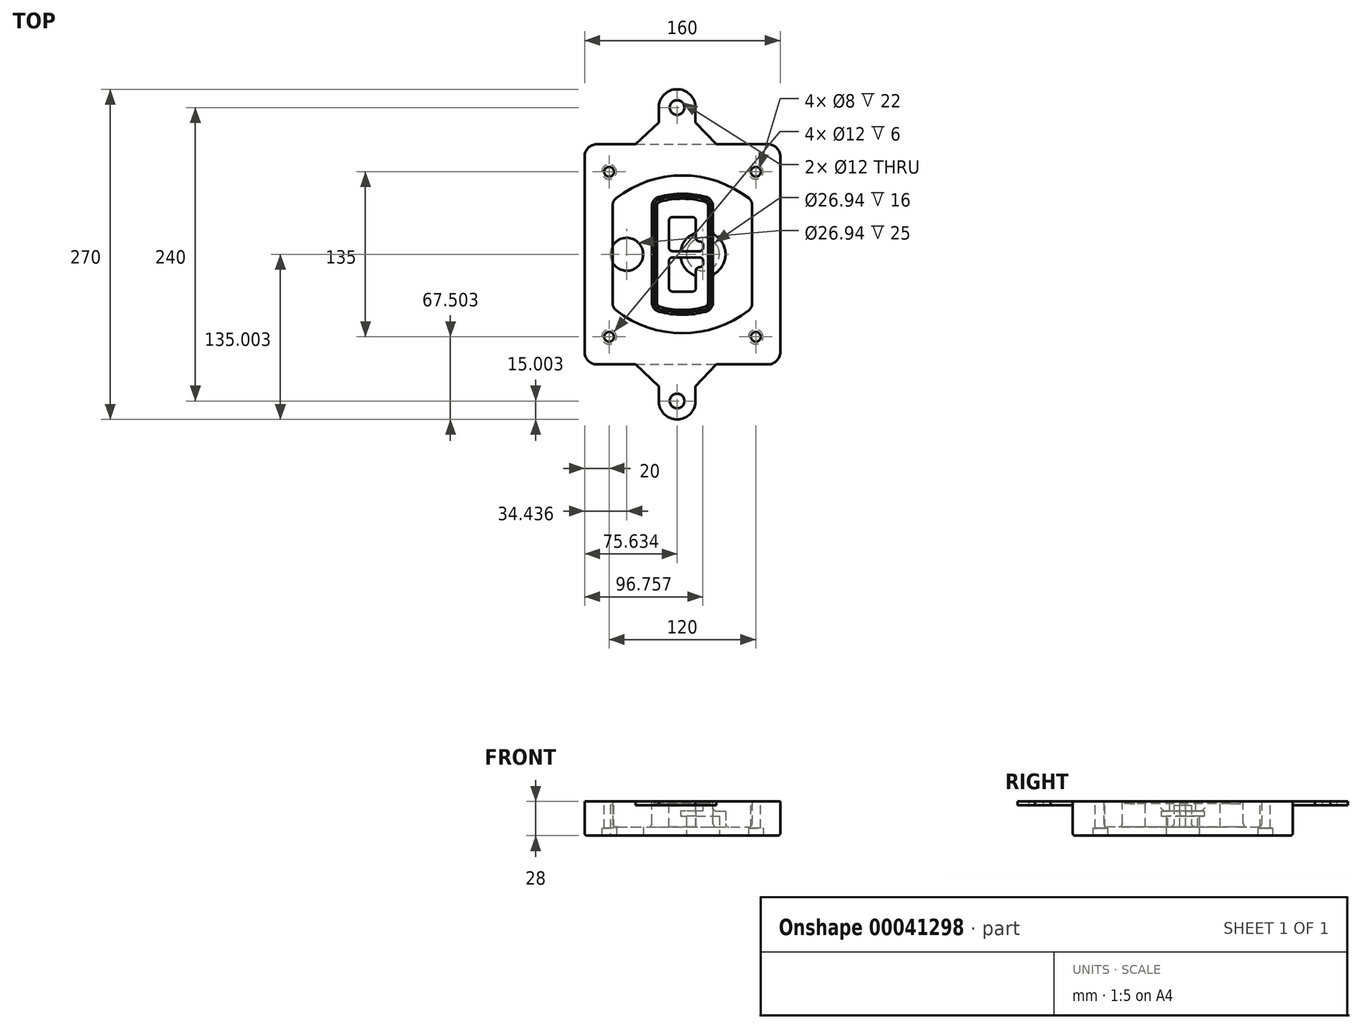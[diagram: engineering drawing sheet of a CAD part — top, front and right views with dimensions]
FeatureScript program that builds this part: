
annotation { "Feature Type Name" : "Feature", "Feature Type Description" : "" }
export const myFeature = defineFeature(function(context is Context, id is Id, definition is map)
    precondition{}
    {
        {
            var Q0;
            Q0=qCreatedBy(makeId("Top.planeOp"),FACE);
            var sketch = newSketch(context, id + "F0", { "sketchPlane" : qUnion([Q0])});
            skPoint(sketch, "E0.rect.middle", {"position": v(0, 0) * mm});
            skLineSegment(sketch, "E1.bottom", {"start": v(24.05, 28.38) * mm, "end": v(164.05, 28.38) * mm});
            skLineSegment(sketch, "E1.top", {"start": v(24.05, 208.38) * mm, "end": v(164.05, 208.38) * mm});
            skLineSegment(sketch, "E1.left", {"start": v(14.05, 38.38) * mm, "end": v(14.05, 198.38) * mm});
            skLineSegment(sketch, "E1.right", {"start": v(174.05, 38.38) * mm, "end": v(174.05, 198.38) * mm});
            skLineSegment(sketch, "E2", {"start": v(14.05, 208.38) * mm, "end": v(174.05, 28.38) * mm, "construction": true});
            skLineSegment(sketch, "E3", {"start": v(174.05, 208.38) * mm, "end": v(14.05, 28.38) * mm, "construction": true});
            skCircle(sketch, "E4", {"center": v(34.05, 185.88) * mm, "radius": 4 * mm});
            skCircle(sketch, "E5", {"center": v(154.05, 185.88) * mm, "radius": 4 * mm});
            skCircle(sketch, "E6", {"center": v(154.05, 50.88) * mm, "radius": 4 * mm});
            skCircle(sketch, "E7", {"center": v(34.05, 50.88) * mm, "radius": 4 * mm});
            skLineSegment(sketch, "E8", {"start": v(34.05, 185.88) * mm, "end": v(154.05, 185.88) * mm, "construction": true});
            skLineSegment(sketch, "E9", {"start": v(154.05, 185.88) * mm, "end": v(154.05, 50.88) * mm, "construction": true});
            skLineSegment(sketch, "E10", {"start": v(154.05, 50.88) * mm, "end": v(34.05, 50.88) * mm, "construction": true});
            skLineSegment(sketch, "E11", {"start": v(34.05, 50.88) * mm, "end": v(34.05, 185.88) * mm, "construction": true});
            skLineSegment(sketch, "E12", {"start": v(34.05, 158.68) * mm, "end": v(34.05, 78.09) * mm});
            skLineSegment(sketch, "E13", {"start": v(154.05, 158.68) * mm, "end": v(154.05, 78.09) * mm});
            skArc(sketch, "E14", {"start": v(150.2, 166.56) * mm, "mid": v(94.05, 185.88) * mm, "end": v(37.9, 166.56) * mm});
            skArc(sketch, "E15", {"start": v(37.9, 70.2) * mm, "mid": v(94.05, 50.88) * mm, "end": v(150.2, 70.2) * mm});
            skLineSegment(sketch, "E16", {"start": v(34.05, 118.38) * mm, "end": v(154.05, 118.38) * mm, "construction": true});
            skPoint(sketch, "E17.visualSharp", {"position": v(34.05, 73.38) * mm});
            skArc(sketch, "E17.filletArc", {"start": v(34.05, 78.09) * mm, "mid": v(35.06, 73.7) * mm, "end": v(37.9, 70.2) * mm});
            skPoint(sketch, "E18.visualSharp", {"position": v(34.05, 163.38) * mm});
            skArc(sketch, "E18.filletArc", {"start": v(37.9, 166.56) * mm, "mid": v(35.06, 163.06) * mm, "end": v(34.05, 158.68) * mm});
            skPoint(sketch, "E19.visualSharp", {"position": v(154.05, 163.38) * mm});
            skArc(sketch, "E19.filletArc", {"start": v(154.05, 158.68) * mm, "mid": v(153.04, 163.06) * mm, "end": v(150.2, 166.56) * mm});
            skPoint(sketch, "E20.visualSharp", {"position": v(154.05, 73.38) * mm});
            skArc(sketch, "E20.filletArc", {"start": v(150.2, 70.2) * mm, "mid": v(153.04, 73.7) * mm, "end": v(154.05, 78.09) * mm});
            skPoint(sketch, "E21.visualSharp", {"position": v(14.05, 208.38) * mm});
            skArc(sketch, "E21.filletArc", {"start": v(24.05, 208.38) * mm, "mid": v(16.98, 205.45) * mm, "end": v(14.05, 198.38) * mm});
            skPoint(sketch, "E22.visualSharp", {"position": v(174.05, 208.38) * mm});
            skArc(sketch, "E22.filletArc", {"start": v(174.05, 198.38) * mm, "mid": v(171.12, 205.45) * mm, "end": v(164.05, 208.38) * mm});
            skPoint(sketch, "E23.visualSharp", {"position": v(174.05, 28.38) * mm});
            skArc(sketch, "E23.filletArc", {"start": v(164.05, 28.38) * mm, "mid": v(171.12, 31.31) * mm, "end": v(174.05, 38.38) * mm});
            skPoint(sketch, "E24.visualSharp", {"position": v(14.05, 28.38) * mm});
            skArc(sketch, "E24.filletArc", {"start": v(14.05, 38.38) * mm, "mid": v(16.98, 31.31) * mm, "end": v(24.05, 28.38) * mm});
            skArc(sketch, "E25.0", {"start": v(151.05, 158.68) * mm, "mid": v(150.34, 161.75) * mm, "end": v(148.36, 164.2) * mm});
            skLineSegment(sketch, "E25.1", {"start": v(151.05, 158.68) * mm, "end": v(151.05, 78.09) * mm});
            skArc(sketch, "E25.2", {"start": v(148.36, 72.57) * mm, "mid": v(150.34, 75.02) * mm, "end": v(151.05, 78.09) * mm});
            skArc(sketch, "E25.3", {"start": v(39.74, 72.57) * mm, "mid": v(94.05, 53.88) * mm, "end": v(148.36, 72.57) * mm});
            skArc(sketch, "E25.4", {"start": v(37.05, 78.09) * mm, "mid": v(37.76, 75.02) * mm, "end": v(39.74, 72.57) * mm});
            skArc(sketch, "E25.5", {"start": v(148.36, 164.2) * mm, "mid": v(94.05, 182.88) * mm, "end": v(39.74, 164.2) * mm});
            skLineSegment(sketch, "E25.6", {"start": v(37.05, 158.68) * mm, "end": v(37.05, 78.09) * mm});
            skArc(sketch, "E25.7", {"start": v(39.74, 164.2) * mm, "mid": v(37.76, 161.75) * mm, "end": v(37.05, 158.68) * mm});
            skArc(sketch, "E26.0", {"start": v(35.43, 169.71) * mm, "mid": v(31.47, 164.82) * mm, "end": v(30.05, 158.68) * mm});
            skArc(sketch, "E26.1", {"start": v(152.67, 169.71) * mm, "mid": v(94.05, 189.88) * mm, "end": v(35.43, 169.71) * mm});
            skArc(sketch, "E26.2", {"start": v(158.05, 158.68) * mm, "mid": v(156.63, 164.82) * mm, "end": v(152.67, 169.71) * mm});
            skLineSegment(sketch, "E26.3", {"start": v(158.05, 158.68) * mm, "end": v(158.05, 78.09) * mm});
            skArc(sketch, "E26.4", {"start": v(152.67, 67.05) * mm, "mid": v(156.63, 71.95) * mm, "end": v(158.05, 78.09) * mm});
            skLineSegment(sketch, "E26.5", {"start": v(30.05, 158.68) * mm, "end": v(30.05, 78.09) * mm});
            skArc(sketch, "E26.6", {"start": v(35.43, 67.05) * mm, "mid": v(94.05, 46.88) * mm, "end": v(152.67, 67.05) * mm});
            skArc(sketch, "E26.7", {"start": v(30.05, 78.09) * mm, "mid": v(31.47, 71.95) * mm, "end": v(35.43, 67.05) * mm});
            skSolve(sketch);
        }
        {
            var Q0;
            Q0=makeQuery(id+"F0.imprint","IMPRINT",FACE,{"disambiguationData":[TD([[makeQuery(id+"F0.imprint","IMPRINT",EDGE,{"derivedFrom":sQuery(id+"F0.wireOp",EDGE,"E1.bottom")}),1.0]])]});
            var Q1;
            Q1=makeQuery(id+"F0.imprint","IMPRINT",FACE,{"disambiguationData":[TD([[makeQuery(id+"F0.imprint","IMPRINT",EDGE,{"derivedFrom":sQuery(id+"F0.wireOp",EDGE,"E12")}),1.0]])]});
            var Q2;
            Q2=makeQuery(id+"F0.imprint","IMPRINT",FACE,{"disambiguationData":[TD([[makeQuery(id+"F0.imprint","IMPRINT",EDGE,{"derivedFrom":sQuery(id+"F0.wireOp",EDGE,"E25.0")}),1.0]])]});
            var Q3;
            Q3=makeQuery(id+"F0.imprint","IMPRINT",FACE,{"disambiguationData":[TD([[makeQuery(id+"F0.imprint","IMPRINT",EDGE,{"derivedFrom":sQuery(id+"F0.wireOp",EDGE,"E12")}),-1.0]])]});
            extrude(context, id + "F1", {"entities" : qUnion([Q0, Q1, Q2, Q3]), "oppositeDirection" : true, "depth" : 25 * mm});
        }
        {
            var Q0;
            Q0=makeQuery(id+"F0.imprint","IMPRINT",FACE,{"disambiguationData":[TD([[makeQuery(id+"F0.imprint","IMPRINT",EDGE,{"derivedFrom":sQuery(id+"F0.wireOp",EDGE,"E12")}),1.0]])]});
            extrude(context, id + "F2", {"entities" : qUnion([Q0]), "operationType" : NewBodyOperationType.ADD, "depth" : 3 * mm});
        }
        {
            var Q0;
            Q0=makeQuery(id+"F0.imprint","IMPRINT",FACE,{"disambiguationData":[TD([[makeQuery(id+"F0.imprint","IMPRINT",EDGE,{"derivedFrom":sQuery(id+"F0.wireOp",EDGE,"E25.0")}),1.0]])]});
            extrude(context, id + "F3", {"entities" : qUnion([Q0]), "operationType" : NewBodyOperationType.REMOVE, "oppositeDirection" : true, "depth" : 18 * mm});
        }
        {
            var Q0;
            Q0=makeQuery(id+"F2.opExtrude","CAP_FACE",FACE,{"disambiguationData":[OSD([sQuery(id+"F0.wireOp",EDGE,"E12"),sQuery(id+"F0.wireOp",EDGE,"E13"),sQuery(id+"F0.wireOp",EDGE,"E14"),sQuery(id+"F0.wireOp",EDGE,"E15"),sQuery(id+"F0.wireOp",EDGE,"E17.filletArc"),sQuery(id+"F0.wireOp",EDGE,"E18.filletArc"),sQuery(id+"F0.wireOp",EDGE,"E19.filletArc"),sQuery(id+"F0.wireOp",EDGE,"E20.filletArc"),sQuery(id+"F0.wireOp",EDGE,"E25.0"),sQuery(id+"F0.wireOp",EDGE,"E25.1"),sQuery(id+"F0.wireOp",EDGE,"E25.2"),sQuery(id+"F0.wireOp",EDGE,"E25.3"),sQuery(id+"F0.wireOp",EDGE,"E25.4"),sQuery(id+"F0.wireOp",EDGE,"E25.5"),sQuery(id+"F0.wireOp",EDGE,"E25.6"),sQuery(id+"F0.wireOp",EDGE,"E25.7")])],"isStart":false});
            var sketch = newSketch(context, id + "F4", { "sketchPlane" : qUnion([Q0])});
            skArc(sketch, "E27.0", {"start": v(74.97, 71.41) * mm, "mid": v(94.05, 68.88) * mm, "end": v(113.13, 71.41) * mm});
            skArc(sketch, "E28.0", {"start": v(113.13, 165.35) * mm, "mid": v(94.05, 167.88) * mm, "end": v(74.97, 165.35) * mm});
            skLineSegment(sketch, "E29", {"start": v(69.05, 157.63) * mm, "end": v(69.05, 79.14) * mm});
            skLineSegment(sketch, "E30", {"start": v(119.05, 157.63) * mm, "end": v(119.05, 79.14) * mm});
            skLineSegment(sketch, "E31", {"start": v(69.05, 163.48) * mm, "end": v(119.05, 163.48) * mm, "construction": true});
            skLineSegment(sketch, "E32", {"start": v(69.05, 73.28) * mm, "end": v(119.05, 73.28) * mm, "construction": true});
            skPoint(sketch, "E33.visualSharp", {"position": v(69.05, 163.48) * mm});
            skArc(sketch, "E33.filletArc", {"start": v(74.97, 165.35) * mm, "mid": v(70.7, 162.5) * mm, "end": v(69.05, 157.63) * mm});
            skPoint(sketch, "E34.visualSharp", {"position": v(119.05, 163.48) * mm});
            skArc(sketch, "E34.filletArc", {"start": v(119.05, 157.63) * mm, "mid": v(117.4, 162.5) * mm, "end": v(113.13, 165.35) * mm});
            skPoint(sketch, "E35.visualSharp", {"position": v(119.05, 73.28) * mm});
            skArc(sketch, "E35.filletArc", {"start": v(113.13, 71.41) * mm, "mid": v(117.4, 74.27) * mm, "end": v(119.05, 79.14) * mm});
            skPoint(sketch, "E36.visualSharp", {"position": v(69.05, 73.28) * mm});
            skArc(sketch, "E36.filletArc", {"start": v(69.05, 79.14) * mm, "mid": v(70.7, 74.27) * mm, "end": v(74.97, 71.41) * mm});
            skArc(sketch, "E37.0", {"start": v(148.36, 164.2) * mm, "mid": v(94.05, 182.88) * mm, "end": v(39.74, 164.2) * mm});
            skArc(sketch, "E37.1", {"start": v(39.74, 164.2) * mm, "mid": v(37.76, 161.75) * mm, "end": v(37.05, 158.68) * mm});
            skLineSegment(sketch, "E37.2", {"start": v(37.05, 158.68) * mm, "end": v(37.05, 78.09) * mm});
            skArc(sketch, "E37.3", {"start": v(37.05, 78.09) * mm, "mid": v(37.76, 75.02) * mm, "end": v(39.74, 72.57) * mm});
            skArc(sketch, "E37.4", {"start": v(39.74, 72.57) * mm, "mid": v(94.05, 53.88) * mm, "end": v(148.36, 72.57) * mm});
            skArc(sketch, "E37.5", {"start": v(148.36, 72.57) * mm, "mid": v(150.34, 75.02) * mm, "end": v(151.05, 78.09) * mm});
            skLineSegment(sketch, "E37.6", {"start": v(151.05, 158.68) * mm, "end": v(151.05, 78.09) * mm});
            skArc(sketch, "E37.7", {"start": v(151.05, 158.68) * mm, "mid": v(150.34, 161.75) * mm, "end": v(148.36, 164.2) * mm});
            skLineSegment(sketch, "E38.0", {"start": v(117.05, 157.63) * mm, "end": v(117.05, 79.14) * mm});
            skArc(sketch, "E38.1", {"start": v(112.61, 73.34) * mm, "mid": v(115.81, 75.49) * mm, "end": v(117.05, 79.14) * mm});
            skArc(sketch, "E38.2", {"start": v(75.49, 73.34) * mm, "mid": v(94.05, 70.88) * mm, "end": v(112.61, 73.34) * mm});
            skArc(sketch, "E38.3", {"start": v(71.05, 79.14) * mm, "mid": v(72.29, 75.49) * mm, "end": v(75.49, 73.34) * mm});
            skLineSegment(sketch, "E38.4", {"start": v(71.05, 157.63) * mm, "end": v(71.05, 79.14) * mm});
            skArc(sketch, "E38.5", {"start": v(117.05, 157.63) * mm, "mid": v(115.81, 161.28) * mm, "end": v(112.61, 163.42) * mm});
            skArc(sketch, "E38.6", {"start": v(75.49, 163.42) * mm, "mid": v(72.29, 161.28) * mm, "end": v(71.05, 157.63) * mm});
            skArc(sketch, "E38.7", {"start": v(112.61, 163.42) * mm, "mid": v(94.05, 165.88) * mm, "end": v(75.49, 163.42) * mm});
            skArc(sketch, "E39.0", {"start": v(115.05, 157.63) * mm, "mid": v(114.23, 160.06) * mm, "end": v(112.1, 161.5) * mm});
            skLineSegment(sketch, "E39.1", {"start": v(115.05, 157.63) * mm, "end": v(115.05, 79.14) * mm});
            skArc(sketch, "E39.2", {"start": v(112.1, 75.27) * mm, "mid": v(114.23, 76.7) * mm, "end": v(115.05, 79.14) * mm});
            skArc(sketch, "E39.3", {"start": v(76, 75.27) * mm, "mid": v(94.05, 72.88) * mm, "end": v(112.1, 75.27) * mm});
            skArc(sketch, "E39.4", {"start": v(73.05, 79.14) * mm, "mid": v(73.87, 76.7) * mm, "end": v(76, 75.27) * mm});
            skArc(sketch, "E39.5", {"start": v(112.1, 161.5) * mm, "mid": v(94.05, 163.88) * mm, "end": v(76, 161.5) * mm});
            skLineSegment(sketch, "E39.6", {"start": v(73.05, 157.63) * mm, "end": v(73.05, 79.14) * mm});
            skArc(sketch, "E39.7", {"start": v(76, 161.5) * mm, "mid": v(73.87, 160.06) * mm, "end": v(73.05, 157.63) * mm});
            skLineSegment(sketch, "E40", {"start": v(69.05, 118.38) * mm, "end": v(119.05, 118.38) * mm, "construction": true});
            skLineSegment(sketch, "E41", {"start": v(83.05, 123.88) * mm, "end": v(83.05, 145.88) * mm});
            skLineSegment(sketch, "E42", {"start": v(86.05, 148.88) * mm, "end": v(102.05, 148.88) * mm});
            skLineSegment(sketch, "E43", {"start": v(105.05, 145.88) * mm, "end": v(105.05, 131.88) * mm});
            skLineSegment(sketch, "E44", {"start": v(108.05, 128.88) * mm, "end": v(108.05, 128.88) * mm});
            skLineSegment(sketch, "E45", {"start": v(111.05, 125.88) * mm, "end": v(111.05, 123.88) * mm});
            skLineSegment(sketch, "E46", {"start": v(108.05, 120.88) * mm, "end": v(86.05, 120.88) * mm});
            skPoint(sketch, "E47.visualSharp", {"position": v(83.05, 148.88) * mm});
            skArc(sketch, "E47.filletArc", {"start": v(86.05, 148.88) * mm, "mid": v(83.93, 148) * mm, "end": v(83.05, 145.88) * mm});
            skPoint(sketch, "E48.visualSharp", {"position": v(105.05, 148.88) * mm});
            skArc(sketch, "E48.filletArc", {"start": v(105.05, 145.88) * mm, "mid": v(104.17, 148) * mm, "end": v(102.05, 148.88) * mm});
            skPoint(sketch, "E49.visualSharp", {"position": v(105.05, 128.88) * mm});
            skArc(sketch, "E49.filletArc", {"start": v(105.05, 131.88) * mm, "mid": v(105.93, 129.76) * mm, "end": v(108.05, 128.88) * mm});
            skPoint(sketch, "E50.visualSharp", {"position": v(111.05, 128.88) * mm});
            skArc(sketch, "E50.filletArc", {"start": v(111.05, 125.88) * mm, "mid": v(110.17, 128) * mm, "end": v(108.05, 128.88) * mm});
            skPoint(sketch, "E51.visualSharp", {"position": v(111.05, 120.88) * mm});
            skArc(sketch, "E51.filletArc", {"start": v(108.05, 120.88) * mm, "mid": v(110.17, 121.76) * mm, "end": v(111.05, 123.88) * mm});
            skPoint(sketch, "E52.visualSharp", {"position": v(83.05, 120.88) * mm});
            skArc(sketch, "E52.filletArc", {"start": v(83.05, 123.88) * mm, "mid": v(83.93, 121.76) * mm, "end": v(86.05, 120.88) * mm});
            skLineSegment(sketch, "E53.0.MirrorCS", {"start": v(108.05, 115.88) * mm, "end": v(86.05, 115.88) * mm});
            skArc(sketch, "E54.0.MirrorCS", {"start": v(83.05, 112.88) * mm, "mid": v(83.93, 115) * mm, "end": v(86.05, 115.88) * mm});
            skLineSegment(sketch, "E55.0.MirrorCS", {"start": v(83.05, 112.88) * mm, "end": v(83.05, 90.88) * mm});
            skArc(sketch, "E56.0.MirrorCS", {"start": v(86.05, 87.88) * mm, "mid": v(83.93, 88.76) * mm, "end": v(83.05, 90.88) * mm});
            skLineSegment(sketch, "E57.0.MirrorCS", {"start": v(86.05, 87.88) * mm, "end": v(102.05, 87.88) * mm});
            skArc(sketch, "E58.0.MirrorCS", {"start": v(105.05, 90.88) * mm, "mid": v(104.17, 88.76) * mm, "end": v(102.05, 87.88) * mm});
            skLineSegment(sketch, "E59.0.MirrorCS", {"start": v(105.05, 90.88) * mm, "end": v(105.05, 104.88) * mm});
            skArc(sketch, "E60.0.MirrorCS", {"start": v(105.05, 104.88) * mm, "mid": v(105.93, 107) * mm, "end": v(108.05, 107.88) * mm});
            skArc(sketch, "E61.0.MirrorCS", {"start": v(111.05, 110.88) * mm, "mid": v(110.17, 108.76) * mm, "end": v(108.05, 107.88) * mm});
            skLineSegment(sketch, "E62.0.MirrorCS", {"start": v(111.05, 110.88) * mm, "end": v(111.05, 112.88) * mm});
            skArc(sketch, "E63.0.MirrorCS", {"start": v(108.05, 115.88) * mm, "mid": v(110.17, 115) * mm, "end": v(111.05, 112.88) * mm});
            skSolve(sketch);
        }
        {
            var Q0;
            Q0=makeQuery(id+"F4.imprint","IMPRINT",FACE,{"disambiguationData":[TD([[makeQuery(id+"F4.imprint","IMPRINT",EDGE,{"derivedFrom":sQuery(id+"F4.wireOp",EDGE,"E27.0")}),1.0]])]});
            var Q1;
            Q1=makeQuery(id+"F4.imprint","IMPRINT",FACE,{"disambiguationData":[TD([[makeQuery(id+"F4.imprint","IMPRINT",EDGE,{"derivedFrom":sQuery(id+"F4.wireOp",EDGE,"E38.0")}),-1.0]])]});
            var Q2;
            Q2=makeQuery(id+"F4.imprint","IMPRINT",FACE,{"disambiguationData":[TD([[makeQuery(id+"F4.imprint","IMPRINT",EDGE,{"derivedFrom":sQuery(id+"F4.wireOp",EDGE,"E39.0")}),1.0]])]});
            extrude(context, id + "F5", {"entities" : qUnion([Q0, Q1, Q2]), "operationType" : NewBodyOperationType.ADD, "endBound" : BoundingType.UP_TO_NEXT, "oppositeDirection" : true, "depth" : 25 * mm});
        }
        {
            var Q0;
            Q0=makeQuery(id+"F4.imprint","IMPRINT",FACE,{"disambiguationData":[TD([[makeQuery(id+"F4.imprint","IMPRINT",EDGE,{"derivedFrom":sQuery(id+"F4.wireOp",EDGE,"E38.0")}),-1.0]])]});
            extrude(context, id + "F6", {"entities" : qUnion([Q0]), "operationType" : NewBodyOperationType.REMOVE, "oppositeDirection" : true, "depth" : 2 * mm});
        }
        {
            var Q0;
            Q0=makeQuery(id+"F1.opExtrude","CAP_FACE",FACE,{"disambiguationData":[OSD([sQuery(id+"F0.wireOp",EDGE,"E1.bottom"),sQuery(id+"F0.wireOp",EDGE,"E1.top"),sQuery(id+"F0.wireOp",EDGE,"E1.left"),sQuery(id+"F0.wireOp",EDGE,"E1.right"),sQuery(id+"F0.wireOp",EDGE,"E4"),sQuery(id+"F0.wireOp",EDGE,"E5"),sQuery(id+"F0.wireOp",EDGE,"E6"),sQuery(id+"F0.wireOp",EDGE,"E7"),sQuery(id+"F0.wireOp",EDGE,"E21.filletArc"),sQuery(id+"F0.wireOp",EDGE,"E22.filletArc"),sQuery(id+"F0.wireOp",EDGE,"E23.filletArc"),sQuery(id+"F0.wireOp",EDGE,"E24.filletArc")])],"isStart":false});
            var sketch = newSketch(context, id + "F7", { "sketchPlane" : qUnion([Q0])});
            skCircle(sketch, "E64", {"center": v(110.8, -118.38) * mm, "radius": 13.47 * mm});
            skCircle(sketch, "E65", {"center": v(48.49, -118.38) * mm, "radius": 13.47 * mm});
            skLineSegment(sketch, "E66", {"start": v(174.05, -118.38) * mm, "end": v(14.05, -118.38) * mm});
            skCircle(sketch, "E67", {"center": v(110.8, -118.38) * mm, "radius": 18.47 * mm});
            skCircle(sketch, "E68", {"center": v(154.05, -185.88) * mm, "radius": 6 * mm});
            skCircle(sketch, "E69", {"center": v(34.05, -185.88) * mm, "radius": 6 * mm});
            skCircle(sketch, "E70", {"center": v(34.05, -50.88) * mm, "radius": 6 * mm});
            skCircle(sketch, "E71", {"center": v(154.05, -50.88) * mm, "radius": 6 * mm});
            skSolve(sketch);
        }
        {
            var Q0;
            {var subQ1=sQuery(id+"F7.wireOp",EDGE,"E66");var subQ4=sQuery(id+"F7.wireOp",EDGE,"E64");var subQ6=makeQuery(id+"F7.imprint","INTERSECT",VERTEX,{"disambiguationData":[OD(0.0)],"derivedFrom":[subQ4,subQ1]});Q0=makeQuery(id+"F7.imprint","IMPRINT",FACE,{"disambiguationData":[TD([[makeQuery(id+"F7.imprint","IMPRINT",EDGE,{"disambiguationData":[TD([[subQ6,-1.0]])],"derivedFrom":subQ4}),-1.0]])]});}
            var Q1;
            {var subQ0=sQuery(id+"F7.wireOp",EDGE,"E66");var subQ1=sQuery(id+"F7.wireOp",EDGE,"E64");var subQ3=makeQuery(id+"F7.imprint","INTERSECT",VERTEX,{"disambiguationData":[OD(0.0)],"derivedFrom":[subQ1,subQ0]});Q1=makeQuery(id+"F7.imprint","IMPRINT",FACE,{"disambiguationData":[TD([[makeQuery(id+"F7.imprint","IMPRINT",EDGE,{"disambiguationData":[TD([[subQ3,-1.0]])],"derivedFrom":subQ1}),1.0]])]});}
            var Q2;
            {var subQ0=sQuery(id+"F7.wireOp",EDGE,"E66");var subQ1=sQuery(id+"F7.wireOp",EDGE,"E64");var subQ3=makeQuery(id+"F7.imprint","INTERSECT",VERTEX,{"disambiguationData":[OD(0.0)],"derivedFrom":[subQ1,subQ0]});Q2=makeQuery(id+"F7.imprint","IMPRINT",FACE,{"disambiguationData":[TD([[makeQuery(id+"F7.imprint","IMPRINT",EDGE,{"disambiguationData":[TD([[subQ3,1.0]])],"derivedFrom":subQ1}),1.0]])]});}
            var Q3;
            {var subQ1=sQuery(id+"F7.wireOp",EDGE,"E66");var subQ4=sQuery(id+"F7.wireOp",EDGE,"E64");var subQ6=makeQuery(id+"F7.imprint","INTERSECT",VERTEX,{"disambiguationData":[OD(0.0)],"derivedFrom":[subQ4,subQ1]});Q3=makeQuery(id+"F7.imprint","IMPRINT",FACE,{"disambiguationData":[TD([[makeQuery(id+"F7.imprint","IMPRINT",EDGE,{"disambiguationData":[TD([[subQ6,1.0]])],"derivedFrom":subQ4}),-1.0]])]});}
            extrude(context, id + "F8", {"entities" : qUnion([Q0, Q1, Q2, Q3]), "operationType" : NewBodyOperationType.ADD, "oppositeDirection" : true, "depth" : 20 * mm});
        }
        {
            var Q0;
            {var subQ0=sQuery(id+"F7.wireOp",EDGE,"E66");var subQ1=sQuery(id+"F7.wireOp",EDGE,"E64");var subQ3=makeQuery(id+"F7.imprint","INTERSECT",VERTEX,{"disambiguationData":[OD(0.0)],"derivedFrom":[subQ1,subQ0]});Q0=makeQuery(id+"F7.imprint","IMPRINT",FACE,{"disambiguationData":[TD([[makeQuery(id+"F7.imprint","IMPRINT",EDGE,{"disambiguationData":[TD([[subQ3,-1.0]])],"derivedFrom":subQ1}),1.0]])]});}
            var Q1;
            {var subQ0=sQuery(id+"F7.wireOp",EDGE,"E66");var subQ1=sQuery(id+"F7.wireOp",EDGE,"E64");var subQ3=makeQuery(id+"F7.imprint","INTERSECT",VERTEX,{"disambiguationData":[OD(0.0)],"derivedFrom":[subQ1,subQ0]});Q1=makeQuery(id+"F7.imprint","IMPRINT",FACE,{"disambiguationData":[TD([[makeQuery(id+"F7.imprint","IMPRINT",EDGE,{"disambiguationData":[TD([[subQ3,1.0]])],"derivedFrom":subQ1}),1.0]])]});}
            extrude(context, id + "F9", {"entities" : qUnion([Q0, Q1]), "operationType" : NewBodyOperationType.REMOVE, "oppositeDirection" : true, "depth" : 16 * mm});
        }
        {
            var Q0;
            {var subQ0=sQuery(id+"F7.wireOp",EDGE,"E66");var subQ1=sQuery(id+"F7.wireOp",EDGE,"E65");var subQ3=makeQuery(id+"F7.imprint","INTERSECT",VERTEX,{"disambiguationData":[OD(0.0)],"derivedFrom":[subQ1,subQ0]});Q0=makeQuery(id+"F7.imprint","IMPRINT",FACE,{"disambiguationData":[TD([[makeQuery(id+"F7.imprint","IMPRINT",EDGE,{"disambiguationData":[TD([[subQ3,-1.0]])],"derivedFrom":subQ1}),1.0]])]});}
            var Q1;
            {var subQ0=sQuery(id+"F7.wireOp",EDGE,"E66");var subQ1=sQuery(id+"F7.wireOp",EDGE,"E65");var subQ3=makeQuery(id+"F7.imprint","INTERSECT",VERTEX,{"disambiguationData":[OD(0.0)],"derivedFrom":[subQ1,subQ0]});Q1=makeQuery(id+"F7.imprint","IMPRINT",FACE,{"disambiguationData":[TD([[makeQuery(id+"F7.imprint","IMPRINT",EDGE,{"disambiguationData":[TD([[subQ3,1.0]])],"derivedFrom":subQ1}),1.0]])]});}
            extrude(context, id + "F10", {"entities" : qUnion([Q0, Q1]), "operationType" : NewBodyOperationType.REMOVE, "oppositeDirection" : true, "depth" : 25 * mm});
        }
        {
            var Q0;
            Q0=makeQuery(id+"F7.imprint","IMPRINT",FACE,{"disambiguationData":[TD([[makeQuery(id+"F7.imprint","IMPRINT",EDGE,{"derivedFrom":sQuery(id+"F7.wireOp",EDGE,"E68")}),1.0]])]});
            var Q1;
            Q1=makeQuery(id+"F7.imprint","IMPRINT",FACE,{"disambiguationData":[TD([[makeQuery(id+"F7.imprint","IMPRINT",EDGE,{"derivedFrom":makeQuery(id+"F1.opExtrude","CAP_EDGE",EDGE,{"disambiguationData":[OSD([sQuery(id+"F0.wireOp",EDGE,"E5")])],"isStart":false})}),-1.0]])]});
            var Q2;
            Q2=makeQuery(id+"F7.imprint","IMPRINT",FACE,{"disambiguationData":[TD([[makeQuery(id+"F7.imprint","IMPRINT",EDGE,{"derivedFrom":sQuery(id+"F7.wireOp",EDGE,"E69")}),1.0]])]});
            var Q3;
            Q3=makeQuery(id+"F7.imprint","IMPRINT",FACE,{"disambiguationData":[TD([[makeQuery(id+"F7.imprint","IMPRINT",EDGE,{"derivedFrom":makeQuery(id+"F1.opExtrude","CAP_EDGE",EDGE,{"disambiguationData":[OSD([sQuery(id+"F0.wireOp",EDGE,"E4")])],"isStart":false})}),-1.0]])]});
            var Q4;
            Q4=makeQuery(id+"F7.imprint","IMPRINT",FACE,{"disambiguationData":[TD([[makeQuery(id+"F7.imprint","IMPRINT",EDGE,{"derivedFrom":sQuery(id+"F7.wireOp",EDGE,"E70")}),1.0]])]});
            var Q5;
            Q5=makeQuery(id+"F7.imprint","IMPRINT",FACE,{"disambiguationData":[TD([[makeQuery(id+"F7.imprint","IMPRINT",EDGE,{"derivedFrom":makeQuery(id+"F1.opExtrude","CAP_EDGE",EDGE,{"disambiguationData":[OSD([sQuery(id+"F0.wireOp",EDGE,"E7")])],"isStart":false})}),-1.0]])]});
            var Q6;
            Q6=makeQuery(id+"F7.imprint","IMPRINT",FACE,{"disambiguationData":[TD([[makeQuery(id+"F7.imprint","IMPRINT",EDGE,{"derivedFrom":sQuery(id+"F7.wireOp",EDGE,"E71")}),1.0]])]});
            var Q7;
            Q7=makeQuery(id+"F7.imprint","IMPRINT",FACE,{"disambiguationData":[TD([[makeQuery(id+"F7.imprint","IMPRINT",EDGE,{"derivedFrom":makeQuery(id+"F1.opExtrude","CAP_EDGE",EDGE,{"disambiguationData":[OSD([sQuery(id+"F0.wireOp",EDGE,"E6")])],"isStart":false})}),-1.0]])]});
            extrude(context, id + "F11", {"entities" : qUnion([Q0, Q1, Q2, Q3, Q4, Q5, Q6, Q7]), "operationType" : NewBodyOperationType.REMOVE, "oppositeDirection" : true, "depth" : 6 * mm});
        }
        {
            var Q0;
            Q0=makeQuery(id+"F9.boolean.opBoolean","COPY",FACE,{"derivedFrom":makeQuery(id+"F9.opExtrude","CAP_FACE",FACE,{"disambiguationData":[OSD([sQuery(id+"F7.wireOp",EDGE,"E64")])],"isStart":false})});
            var sketch = newSketch(context, id + "F12", { "sketchPlane" : qUnion([Q0])});
            skArc(sketch, "E72.0", {"start": v(105.05, -100.83) * mm, "mid": v(96.62, -106.56) * mm, "end": v(92.5, -115.88) * mm});
            skArc(sketch, "E72.1", {"start": v(92.5, -120.88) * mm, "mid": v(96.62, -130.2) * mm, "end": v(105.05, -135.93) * mm});
            skLineSegment(sketch, "E73", {"start": v(92.5, -120.88) * mm, "end": v(108.05, -120.88) * mm});
            skLineSegment(sketch, "E74.0", {"start": v(108.05, -115.88) * mm, "end": v(92.5, -115.88) * mm});
            skArc(sketch, "E74.1", {"start": v(108.05, -115.88) * mm, "mid": v(110.17, -115) * mm, "end": v(111.05, -112.88) * mm});
            skLineSegment(sketch, "E74.2", {"start": v(111.05, -110.88) * mm, "end": v(111.05, -112.88) * mm});
            skArc(sketch, "E74.3", {"start": v(111.05, -110.88) * mm, "mid": v(110.17, -108.76) * mm, "end": v(108.05, -107.88) * mm});
            skArc(sketch, "E74.4", {"start": v(105.05, -104.88) * mm, "mid": v(105.93, -107) * mm, "end": v(108.05, -107.88) * mm});
            skLineSegment(sketch, "E74.5", {"start": v(105.05, -100.83) * mm, "end": v(105.05, -104.88) * mm});
            skLineSegment(sketch, "E74.7", {"start": v(108.05, -120.88) * mm, "end": v(92.5, -120.88) * mm});
            skArc(sketch, "E74.8", {"start": v(108.05, -120.88) * mm, "mid": v(110.17, -121.76) * mm, "end": v(111.05, -123.88) * mm});
            skLineSegment(sketch, "E74.9", {"start": v(111.05, -125.88) * mm, "end": v(111.05, -123.88) * mm});
            skArc(sketch, "E74.10", {"start": v(111.05, -125.88) * mm, "mid": v(110.17, -128) * mm, "end": v(108.05, -128.88) * mm});
            skArc(sketch, "E74.11", {"start": v(105.05, -131.88) * mm, "mid": v(105.93, -129.76) * mm, "end": v(108.05, -128.88) * mm});
            skLineSegment(sketch, "E74.12", {"start": v(105.05, -135.93) * mm, "end": v(105.05, -131.88) * mm});
            skPoint(sketch, "E75.orphan", {"position": v(105.05, -145.88) * mm});
            skPoint(sketch, "E76.orphan", {"position": v(86.05, -120.88) * mm});
            skPoint(sketch, "E77.orphan", {"position": v(86.05, -115.88) * mm});
            skPoint(sketch, "E78.orphan", {"position": v(105.05, -90.88) * mm});
            skSolve(sketch);
        }
        {
            var Q0;
            {var subQ7=sQuery(id+"F12.wireOp",EDGE,"E72.0");var subQ14=sQuery(id+"F12.wireOp",EDGE,"E72.1");var subQ16=sQuery(id+"F12.wireOp",EDGE,"E74.1");var subQ18=sQuery(id+"F12.wireOp",EDGE,"E74.8");Q0=qUnion([makeQuery(id+"F12.imprint","IMPRINT",FACE,{"disambiguationData":[TD([[makeQuery(id+"F12.imprint","IMPRINT",EDGE,{"derivedFrom":subQ7}),1.0]])]}),makeQuery(id+"F12.imprint","IMPRINT",FACE,{"disambiguationData":[TD([[makeQuery(id+"F12.imprint","IMPRINT",EDGE,{"derivedFrom":subQ14}),1.0]])]}),makeQuery(id+"F12.imprint","IMPRINT",FACE,{"disambiguationData":[TD([[makeQuery(id+"F12.imprint","IMPRINT",EDGE,{"derivedFrom":subQ16}),1.0]])]}),makeQuery(id+"F12.imprint","IMPRINT",FACE,{"disambiguationData":[TD([[makeQuery(id+"F12.imprint","IMPRINT",EDGE,{"derivedFrom":subQ18}),-1.0]])]})]);}
            var Q1;
            Q1=makeQuery(id+"F5.boolean.opBoolean","SPLIT",FACE,{"disambiguationData":[TD([makeQuery(id+"F5.opExtrude","SWEPT_FACE",FACE,{"disambiguationData":[OSD([sQuery(id+"F4.wireOp",EDGE,"E41")])]})])],"derivedFrom":makeQuery(id+"F3.boolean.opBoolean","COPY",FACE,{"derivedFrom":makeQuery(id+"F3.opExtrude","CAP_FACE",FACE,{"disambiguationData":[OSD([sQuery(id+"F0.wireOp",EDGE,"E25.0"),sQuery(id+"F0.wireOp",EDGE,"E25.1"),sQuery(id+"F0.wireOp",EDGE,"E25.2"),sQuery(id+"F0.wireOp",EDGE,"E25.3"),sQuery(id+"F0.wireOp",EDGE,"E25.4"),sQuery(id+"F0.wireOp",EDGE,"E25.5"),sQuery(id+"F0.wireOp",EDGE,"E25.6"),sQuery(id+"F0.wireOp",EDGE,"E25.7")])],"isStart":false})})});
            extrude(context, id + "F13", {"entities" : qUnion([Q0]), "operationType" : NewBodyOperationType.REMOVE, "endBound" : BoundingType.UP_TO_SURFACE, "endBoundEntityFace" : qUnion([Q1]), "depth" : 25 * mm});
        }
        {
            var Q0;
            Q0=makeQuery(id+"F3.boolean.opBoolean","COPY",EDGE,{"derivedFrom":makeQuery(id+"F3.opExtrude","CAP_EDGE",EDGE,{"disambiguationData":[OSD([sQuery(id+"F0.wireOp",EDGE,"E25.6")])],"isStart":false})});
            var Q1;
            Q1=makeQuery(id+"F8.boolean.opBoolean","INTERSECT",EDGE,{"derivedFrom":[makeQuery(id+"F5.opExtrude","SWEPT_FACE",FACE,{"disambiguationData":[OSD([sQuery(id+"F4.wireOp",EDGE,"E30")])]}),makeQuery(id+"F8.opExtrude","CAP_FACE",FACE,{"disambiguationData":[OSD([sQuery(id+"F7.wireOp",EDGE,"E67")])],"isStart":false})]});
            var Q2;
            Q2=makeQuery(id+"F8.boolean.opBoolean","INTERSECT",EDGE,{"disambiguationData":[OD(1.0)],"derivedFrom":[makeQuery(id+"F5.opExtrude","SWEPT_FACE",FACE,{"disambiguationData":[OSD([sQuery(id+"F4.wireOp",EDGE,"E30")])]}),makeQuery(id+"F8.opExtrude","SWEPT_FACE",FACE,{"disambiguationData":[OSD([sQuery(id+"F7.wireOp",EDGE,"E67")])]})]});
            var Q3;
            {var subQ0=sQuery(id+"F4.wireOp",EDGE,"E30");Q3=makeQuery(id+"F8.boolean.opBoolean","SPLIT",EDGE,{"disambiguationData":[TD([makeQuery(id+"F5.opExtrude","SWEPT_FACE",FACE,{"disambiguationData":[OSD([sQuery(id+"F4.wireOp",EDGE,"E35.filletArc")])]})])],"derivedFrom":makeQuery(id+"F5.opExtrude","CAP_EDGE",EDGE,{"disambiguationData":[OSD([subQ0])],"isStart":false})});}
            var Q4;
            {var subQ0=sQuery(id+"F0.wireOp",EDGE,"E25.7");var subQ1=sQuery(id+"F0.wireOp",EDGE,"E25.1");var subQ2=sQuery(id+"F0.wireOp",EDGE,"E25.6");var subQ3=sQuery(id+"F0.wireOp",EDGE,"E25.5");var subQ4=sQuery(id+"F0.wireOp",EDGE,"E25.4");var subQ5=sQuery(id+"F0.wireOp",EDGE,"E25.0");var subQ6=sQuery(id+"F0.wireOp",EDGE,"E25.2");var subQ7=sQuery(id+"F0.wireOp",EDGE,"E25.3");Q4=makeQuery(id+"F8.boolean.opBoolean","INTERSECT",EDGE,{"derivedFrom":[makeQuery(id+"F5.boolean.opBoolean","SPLIT",FACE,{"disambiguationData":[TD([makeQuery(id+"F2.opExtrude","SWEPT_FACE",FACE,{"disambiguationData":[OSD([subQ5])]})])],"derivedFrom":makeQuery(id+"F3.boolean.opBoolean","COPY",FACE,{"derivedFrom":makeQuery(id+"F3.opExtrude","CAP_FACE",FACE,{"disambiguationData":[OSD([subQ5,subQ1,subQ6,subQ7,subQ4,subQ3,subQ2,subQ0])],"isStart":false})})}),makeQuery(id+"F8.opExtrude","SWEPT_FACE",FACE,{"disambiguationData":[OSD([sQuery(id+"F7.wireOp",EDGE,"E67")])]})]});}
            var Q5;
            Q5=makeQuery(id+"F8.boolean.opBoolean","INTERSECT",EDGE,{"disambiguationData":[OD(0.0)],"derivedFrom":[makeQuery(id+"F5.opExtrude","SWEPT_FACE",FACE,{"disambiguationData":[OSD([sQuery(id+"F4.wireOp",EDGE,"E30")])]}),makeQuery(id+"F8.opExtrude","SWEPT_FACE",FACE,{"disambiguationData":[OSD([sQuery(id+"F7.wireOp",EDGE,"E67")])]})]});
            fillet(context, id + "F14", {"entities" : qUnion([Q0, Q1, Q2, Q3, Q4, Q5]), "radius" : 3 * mm, "tangentPropagation" : true, "allowEdgeOverflow" : false});
        }
        {
            var Q0;
            Q0=makeQuery(id+"F1.opExtrude","CAP_EDGE",EDGE,{"disambiguationData":[OSD([sQuery(id+"F0.wireOp",EDGE,"E1.bottom")])],"isStart":false});
            fillet(context, id + "F15", {"entities" : qUnion([Q0]), "radius" : 2 * mm, "tangentPropagation" : true, "allowEdgeOverflow" : false});
        }
        {
            var Q0;
            {var subQ0=sQuery(id+"F0.wireOp",EDGE,"E1.bottom");var subQ1=sQuery(id+"F0.wireOp",EDGE,"E1.top");var subQ2=sQuery(id+"F0.wireOp",EDGE,"E1.left");var subQ3=sQuery(id+"F0.wireOp",EDGE,"E1.right");var subQ4=sQuery(id+"F0.wireOp",EDGE,"E4");var subQ5=sQuery(id+"F0.wireOp",EDGE,"E5");var subQ6=sQuery(id+"F0.wireOp",EDGE,"E6");var subQ7=sQuery(id+"F0.wireOp",EDGE,"E7");var subQ8=sQuery(id+"F0.wireOp",EDGE,"E21.filletArc");var subQ9=sQuery(id+"F0.wireOp",EDGE,"E22.filletArc");var subQ10=sQuery(id+"F0.wireOp",EDGE,"E23.filletArc");var subQ11=sQuery(id+"F0.wireOp",EDGE,"E24.filletArc");Q0=makeQuery(id+"F2.boolean.opBoolean","SPLIT",FACE,{"disambiguationData":[TD([makeQuery(id+"F1.opExtrude","SWEPT_FACE",FACE,{"disambiguationData":[OSD([subQ0])]})])],"derivedFrom":makeQuery(id+"F1.opExtrude","CAP_FACE",FACE,{"disambiguationData":[OSD([subQ0,subQ1,subQ2,subQ3,subQ4,subQ5,subQ6,subQ7,subQ8,subQ9,subQ10,subQ11])],"isStart":true})});}
            var sketch = newSketch(context, id + "F16", { "sketchPlane" : qUnion([Q0])});
            skSolve(sketch);
        }
        {
            var Q0;
            Q0=makeQuery(id+"F16.imprint","IMPRINT",FACE,{"disambiguationData":[TD([[makeQuery(id+"F16.imprint","IMPRINT",EDGE,{"derivedFrom":makeQuery(id+"F1.opExtrude","CAP_EDGE",EDGE,{"disambiguationData":[OSD([sQuery(id+"F0.wireOp",EDGE,"E1.bottom")])],"isStart":true})}),1.0]])]});
            var sketch = newSketch(context, id + "F17", { "sketchPlane" : qUnion([Q0])});
            skLineSegment(sketch, "E79", {"start": v(55.87, 208.38) * mm, "end": v(74.7, 226.38) * mm});
            skLineSegment(sketch, "E80", {"start": v(74.7, 226.38) * mm, "end": v(74.7, 239.07) * mm});
            skLineSegment(sketch, "E81", {"start": v(121.87, 208.38) * mm, "end": v(104.67, 226.38) * mm});
            skLineSegment(sketch, "E82", {"start": v(104.67, 226.38) * mm, "end": v(104.67, 239.07) * mm});
            skArc(sketch, "E83", {"start": v(104.67, 239.07) * mm, "mid": v(89.68, 253.38) * mm, "end": v(74.7, 239.07) * mm});
            skCircle(sketch, "E84", {"center": v(89.68, 238.38) * mm, "radius": 6 * mm});
            skLineSegment(sketch, "E85", {"start": v(89.68, 238.38) * mm, "end": v(89.68, 208.38) * mm, "construction": true});
            skLineSegment(sketch, "E86", {"start": v(13.27, 118.38) * mm, "end": v(162.6, 118.38) * mm, "construction": true});
            skLineSegment(sketch, "E87.MirrorCS", {"start": v(55.87, 28.38) * mm, "end": v(74.7, 10.38) * mm});
            skLineSegment(sketch, "E88.MirrorCS", {"start": v(74.7, 10.38) * mm, "end": v(74.7, -2.3) * mm});
            skLineSegment(sketch, "E89.MirrorCS", {"start": v(121.87, 28.38) * mm, "end": v(104.67, 10.38) * mm});
            skLineSegment(sketch, "E90.MirrorCS", {"start": v(104.67, 10.38) * mm, "end": v(104.67, -2.3) * mm});
            skArc(sketch, "E91.MirrorCS", {"start": v(104.67, -2.3) * mm, "mid": v(89.68, -16.62) * mm, "end": v(74.7, -2.3) * mm});
            skCircle(sketch, "E92.MirrorC", {"center": v(89.68, -1.62) * mm, "radius": 6 * mm});
            skLineSegment(sketch, "E93.MirrorCS", {"start": v(89.68, -1.62) * mm, "end": v(89.68, 28.38) * mm, "construction": true});
            skSolve(sketch);
        }
        {
            var Q0;
            Q0=makeQuery(id+"F16.imprint","IMPRINT",FACE,{"disambiguationData":[TD([[makeQuery(id+"F16.imprint","IMPRINT",EDGE,{"derivedFrom":makeQuery(id+"F1.opExtrude","CAP_EDGE",EDGE,{"disambiguationData":[OSD([sQuery(id+"F0.wireOp",EDGE,"E1.bottom")])],"isStart":true})}),1.0]])]});
            var Q1;
            {var subQ2=sQuery(id+"F17.wireOp",EDGE,"E87.MirrorCS");Q1=makeQuery(id+"F17.imprint","IMPRINT",FACE,{"disambiguationData":[TD([[makeQuery(id+"F17.imprint","IMPRINT",EDGE,{"derivedFrom":subQ2}),1.0]])]});}
            var Q2;
            {var subQ2=sQuery(id+"F17.wireOp",EDGE,"E79");Q2=makeQuery(id+"F17.imprint","IMPRINT",FACE,{"disambiguationData":[TD([[makeQuery(id+"F17.imprint","IMPRINT",EDGE,{"derivedFrom":subQ2}),-1.0]])]});}
            var Q3;
            Q3=makeQuery(id+"F2.opExtrude","CAP_FACE",FACE,{"disambiguationData":[OSD([sQuery(id+"F0.wireOp",EDGE,"E12"),sQuery(id+"F0.wireOp",EDGE,"E13"),sQuery(id+"F0.wireOp",EDGE,"E14"),sQuery(id+"F0.wireOp",EDGE,"E15"),sQuery(id+"F0.wireOp",EDGE,"E17.filletArc"),sQuery(id+"F0.wireOp",EDGE,"E18.filletArc"),sQuery(id+"F0.wireOp",EDGE,"E19.filletArc"),sQuery(id+"F0.wireOp",EDGE,"E20.filletArc"),sQuery(id+"F0.wireOp",EDGE,"E25.0"),sQuery(id+"F0.wireOp",EDGE,"E25.1"),sQuery(id+"F0.wireOp",EDGE,"E25.2"),sQuery(id+"F0.wireOp",EDGE,"E25.3"),sQuery(id+"F0.wireOp",EDGE,"E25.4"),sQuery(id+"F0.wireOp",EDGE,"E25.5"),sQuery(id+"F0.wireOp",EDGE,"E25.6"),sQuery(id+"F0.wireOp",EDGE,"E25.7")])],"isStart":false});
            extrude(context, id + "F18", {"entities" : qUnion([Q0, Q1, Q2]), "operationType" : NewBodyOperationType.ADD, "endBound" : BoundingType.UP_TO_SURFACE, "endBoundEntityFace" : qUnion([Q3]), "depth" : 25 * mm});
        }
    });
